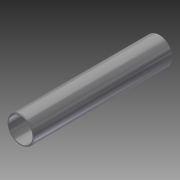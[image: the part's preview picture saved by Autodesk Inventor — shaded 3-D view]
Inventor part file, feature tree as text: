
AUTODESK INVENTOR PART (.ipt)
format: ipt  version: 2014 SP1 (Build 180222100, 222)  size: 103,936 bytes
history: native  units: in
note: dims shown in document units (in); Inventor stores cm internally (conversion verified against a paired STEP export)
features: sketch x2, extrude x1, revolve x1, mirror x1
ambient origin geometry x8: Origin, YZ Plane, XZ Plane, XY Plane, X Axis, Y Axis, Z Axis, Center Point
bodies: Solid1 (feature_tree)
feature tree (5):
  extrude  "Extrusion1"  Depth=0.1in
  revolve  "Revolution1"  [1 undecoded]
  mirror  "Mirror1"
  sketch  "Sketch1"  dims[d0=2.062in d1=0.1in]
  sketch  "Sketch2"  dims[d2=10.72in d3=0.0in d4=0.0625in d5=0.031in d6=90.0deg]
note: 1 required parameter value undecoded (feature->parameter linkage not recoverable at this tier; creation-order binding heuristic only, values carry confidence <= 0.55)
